# Revit family: ToiletPartition_ASI_Alpaco-Kids
name_source: partatom
category: Casework
revit_build: Autodesk Revit 2014 (Build: 20140709_2115(x64)
units: mm (PartAtom-declared; Revit-internal decimal feet)

## types (6) — shared parameters
Assembly Code = C1010400
Construction Details = http://www.arcat.com
Description = Partition as Specified in 10 21 00
Door Handle Height = 3' - 0"
Door Height = 4' - 1 7/32"
Door Style = Door : Kids
Door Thickness = 0' - 0 1/2"
FootLoc_Hinge = 0' - 3"
FootLoc_Strike = 0' - 3"
Green Building-LEED = http://www.arcat.com
Headrail Height = 0' - 1 1/4"
Height = 6' - 8 5/16"
Installation-Fabrication = http://www.accuratepartitions.com
Keynote = 10 21 00
Manufacturer = Accurate Partitions Corp
Manufacturer Fax = 708-442-7439
Manufacturer Website = http://www.accuratepartitions.com
Model = As Specified in 10 21 00
Panel - Hinge Side = Pilaster : End Panel
Panel Height = 4' - 1 7/32"
Panel Height from Floor = 0' - 5 29/32"
Panel Thickness = 0' - 0 1/2"
Pilaster Height = 6' - 7 3/8"
Pilaster Thickness = 0' - 0 1/2"
Product Data = http://www.arcat.com
Product Properties = http://www.arcat.com
Revision = R1_09-2010
Sales Information = http://www.accuratepartitions.com
Send Message = http://www.arcat.com
Specification = http://www.arcat.com
Strike Pilaster = Yes
Test Data = http://www.accuratepartitions.com
Type Comments = Contact Manufacturer for More Information
URL = http://www.accuratepartitions.com
zero-valued in all types: Expected Lifespan (Years), Maintenance Schedule (Months), Warranty Duration (Years)

## per-type parameters (varying)
| type | 2Feet_HingeSide | 2Feet_StrikeSide | Foot Space_Hinge | Foot Space_Strike | FrontRailOnly | GapHng | GapStrk | Has Return Rail 1 | Has Return Rail2 | HasBothReturns | Hinge Pilaster | Hinge Side Panel | HngPilast2 | HngPnlOffset | Offset Hinge Panel | Offset Strike Panel | Panel - Strike Side | Pilaster Width_Hinge Side | Pilaster Width_Strike Side | Strike Side Panel | StrkPilast2 | StrkPnlOffset |
| First Stall - Hinge Side At Wall | No | Yes | 0' - 3" | 0' - 6" | Yes | 0' - 1 1/4" | 0' - 0" | No | No | No | Yes | No | 0' - 3" | 0' - 6 1/4" | Yes | No | Pilaster : Mid Panel | 0' - 6" | 1' - 0" | Yes | 0' - 6" | 0' - 6" |
| Intermediate Stall | No | Yes | 0' - 3" | 0' - 6" | Yes | 0' - 1 1/4" | 0' - 0" | No | No | No | No | No | 0' - 3" | 0' - 6 1/4" | Yes | No | Pilaster : Mid Panel | 0' - 6" | 1' - 0" | Yes | 0' - 6" | 0' - 6" |
| First Stall - Strike Side At Wall | Yes | No | 0' - 6" | 0' - 3" | Yes | 0' - 0" | 0' - 1 1/4" | No | No | No | No | No | 0' - 6" | 0' - 6" | No | Yes | Pilaster : Mid Panel | 1' - 0" | 0' - 6" | No | 0' - 3" | 0' - 6 1/4" |
| Single Stall - Freestanding | No | No | 0' - 3" | 0' - 3" | No | 0' - 1 1/4" | 0' - 1 1/4" | Yes | Yes | Yes | Yes | Yes | 0' - 3" | 0' - 6 1/4" | Yes | Yes | Pilaster : End Panel | 0' - 6" | 0' - 6" | Yes | 0' - 3" | 0' - 6 1/4" |
| Last Stall - Strike Side Panel | No | No | 0' - 3" | 0' - 3" | No | 0' - 1 1/4" | 0' - 1 1/4" | No | Yes | No | No | No | 0' - 3" | 0' - 6 1/4" | Yes | Yes | Pilaster : End Panel | 0' - 6" | 0' - 6" | Yes | 0' - 3" | 0' - 6 1/4" |
| Last Stall - Hinge Side Panel | No | Yes | 0' - 3" | 0' - 6" | No | 0' - 1 1/4" | 0' - 0" | Yes | No | No | Yes | Yes | 0' - 3" | 0' - 6 1/4" | Yes | No | Pilaster : Mid Panel | 0' - 6" | 1' - 0" | Yes | 0' - 6" | 0' - 6" |

## geometry (parser evidence)
native form markers: Sweep x12
no freeform markers — native parametric forms only
